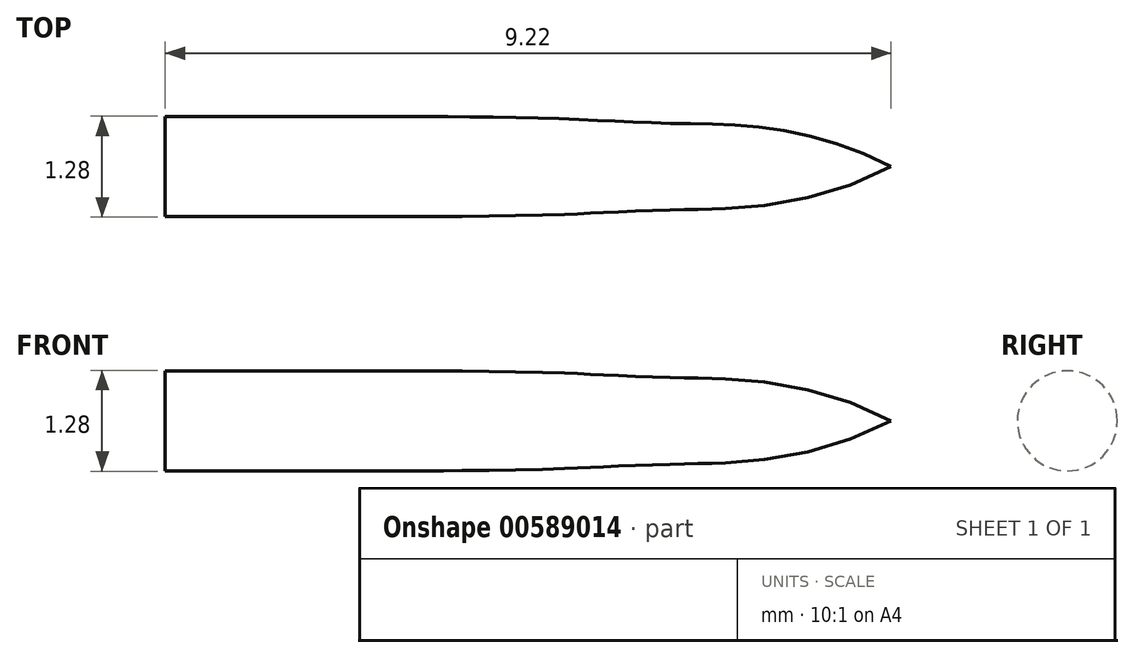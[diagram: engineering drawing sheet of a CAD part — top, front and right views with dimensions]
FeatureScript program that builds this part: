
annotation { "Feature Type Name" : "Feature", "Feature Type Description" : "" }
export const myFeature = defineFeature(function(context is Context, id is Id, definition is map)
    precondition{}
    {
        {
            var Q0;
            Q0=qCreatedBy(makeId("Top.planeOp"),FACE);
            var sketch = newSketch(context, id + "F0", { "sketchPlane" : qUnion([Q0])});
            skLineSegment(sketch, "E0", {"start": v(0, 0) * mm, "end": v(10.16, 0) * mm});
            skFitSpline(sketch, "E1", {"points": [v(-2.52, 1.27) * mm, v(1.44, 1.23) * mm, v(4.6, 1.1) * mm, v(10.16, 0) * mm], "startDerivative": vector(8.47, 0) * mm, "endDerivative": vector(16.36, -8.68) * mm});
            skLineSegment(sketch, "E2", {"start": v(0, 0) * mm, "end": v(-8.29, 0) * mm});
            skLineSegment(sketch, "E3", {"start": v(-8.29, 0) * mm, "end": v(-8.29, 1.27) * mm});
            skLineSegment(sketch, "E4", {"start": v(-8.29, 1.27) * mm, "end": v(-2.52, 1.27) * mm});
            skSolve(sketch);
        }
        {
            var Q0;
            Q0=makeQuery(id+"F0.imprint","IMPRINT",FACE,{"disambiguationData":[TD([[makeQuery(id+"F0.imprint","IMPRINT",EDGE,{"derivedFrom":sQuery(id+"F0.wireOp",EDGE,"E0")}),1.0]])]});
            var Q1;
            Q1=sQuery(id+"F0.wireOp",EDGE,"E0");
            revolve(context, id + "F1", {"entities" : qUnion([Q0]), "axis" : qUnion([Q1]), "revolveType" : RevolveType.FULL});
        }
        {
            var Q0;
            Q0=makeQuery(id+"F1.opRevolve","SWEPT_BODY",BODY,{"disambiguationData":[OSD([sQuery(id+"F0.wireOp",EDGE,"E0"),sQuery(id+"F0.wireOp",EDGE,"TRYClLdt-NgUj-KORk-zrvL-jfI83vSRoGs2"),sQuery(id+"F0.wireOp",EDGE,"E1")])]});
            var Q1;
            Q1=qCreatedBy(makeId("Origin.pointOp"),VERTEX);
            transform(context, id + "F2", {"entities" : qUnion([Q0]), "transformType" : TransformType.SCALE_UNIFORMLY, "scale" : .5, "scalePoint" : qUnion([Q1]), "makeCopy" : false});
        }
    });
